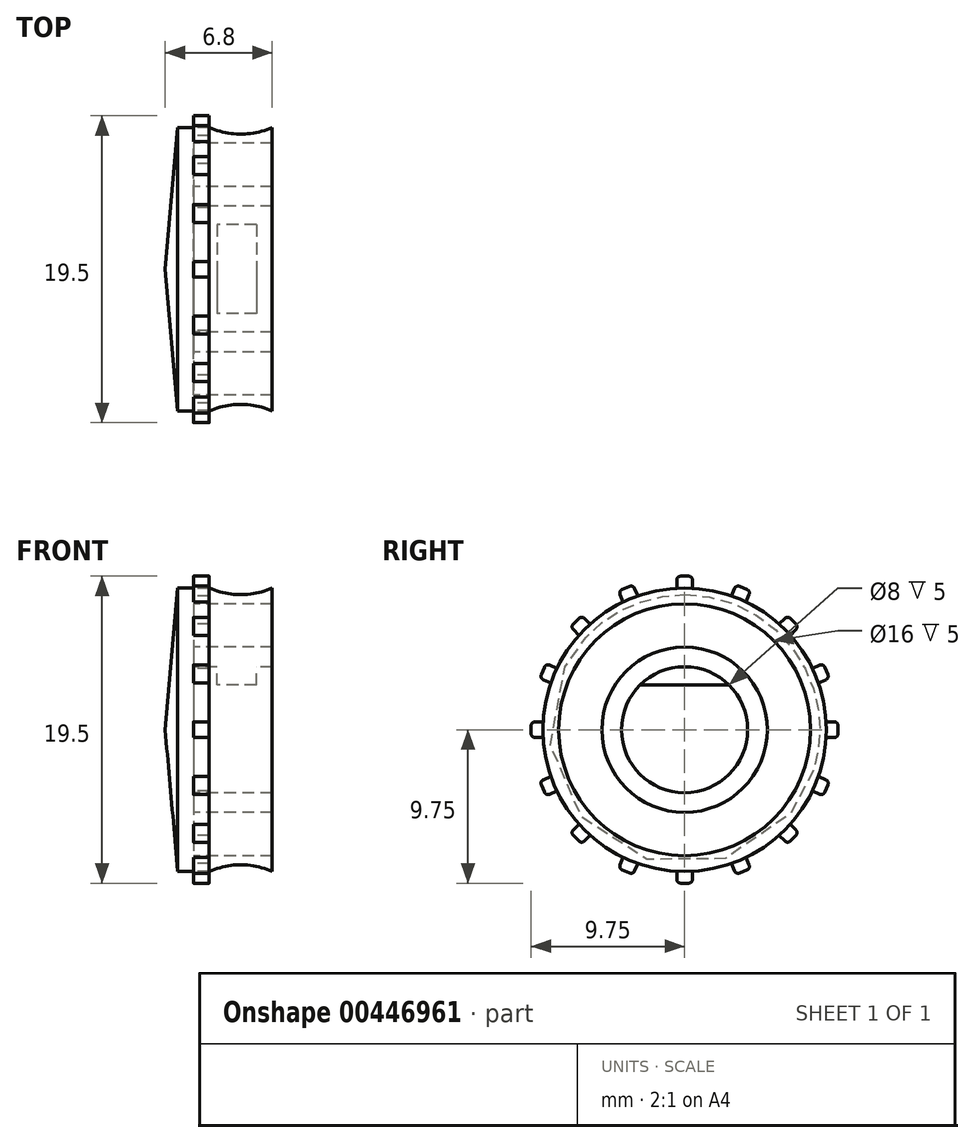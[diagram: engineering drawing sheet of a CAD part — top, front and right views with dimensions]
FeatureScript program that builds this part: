
annotation { "Feature Type Name" : "Feature", "Feature Type Description" : "" }
export const myFeature = defineFeature(function(context is Context, id is Id, definition is map)
    precondition{}
    {
        {
            var Q0;
            Q0=qCreatedBy(makeId("Front.planeOp"),FACE);
            var sketch = newSketch(context, id + "F0", { "sketchPlane" : qUnion([Q0])});
            skLineSegment(sketch, "E0", {"start": v(0, 0) * mm, "end": v(10, 0) * mm, "construction": true});
            skLineSegment(sketch, "E1", {"start": v(-1, 9) * mm, "end": v(0, 9) * mm});
            skLineSegment(sketch, "E2", {"start": v(5, 0) * mm, "end": v(5, 168.85) * mm, "construction": true});
            skLineSegment(sketch, "E3.top", {"start": v(5, 5.25) * mm, "end": v(0, 5.25) * mm});
            skLineSegment(sketch, "E3.left", {"start": v(5, 5.25) * mm, "end": v(5, 4) * mm});
            skLineSegment(sketch, "E4", {"start": v(1, 9) * mm, "end": v(1, 9) * mm});
            skLineSegment(sketch, "E5", {"start": v(1, 9) * mm, "end": v(9, 9) * mm, "construction": true});
            skLineSegment(sketch, "E6", {"start": v(9, 9) * mm, "end": v(41.44, 9) * mm, "construction": true});
            skLineSegment(sketch, "E7", {"start": v(0, 5.25) * mm, "end": v(0, 0) * mm});
            skLineSegment(sketch, "E8", {"start": v(0, 4) * mm, "end": v(0, -2.16) * mm});
            skLineSegment(sketch, "E9", {"start": v(0, 4) * mm, "end": v(5, 4) * mm});
            skLineSegment(sketch, "E10", {"start": v(0, 8) * mm, "end": v(0, 4) * mm});
            skLineSegment(sketch, "E11", {"start": v(0, 0) * mm, "end": v(-1.8, 0) * mm});
            skLineSegment(sketch, "E12", {"start": v(0, 0) * mm, "end": v(0, 37.74) * mm, "construction": true});
            skLineSegment(sketch, "E13", {"start": v(0, 9) * mm, "end": v(1, 9) * mm});
            skLineSegment(sketch, "E14", {"start": v(-1, 9) * mm, "end": v(-1.8, 0) * mm});
            skLineSegment(sketch, "E15", {"start": v(0, 8) * mm, "end": v(5, 8) * mm});
            skLineSegment(sketch, "E16", {"start": v(5, 8) * mm, "end": v(5, 9) * mm});
            skArc(sketch, "E17", {"start": v(1, 9) * mm, "mid": v(3, 8.58) * mm, "end": v(5, 9) * mm});
            skLineSegment(sketch, "E18.top", {"start": v(0, 10.5) * mm, "end": v(1, 10.5) * mm});
            skLineSegment(sketch, "E18.left", {"start": v(0, 9) * mm, "end": v(0, 10.5) * mm});
            skLineSegment(sketch, "E18.right", {"start": v(1, 9) * mm, "end": v(1, 10.5) * mm});
            skSolve(sketch);
        }
        {
            var Q0;
            Q0=makeQuery(id+"F0.imprint","IMPRINT",FACE,{"disambiguationData":[TD([[makeQuery(id+"F0.imprint","IMPRINT",EDGE,{"derivedFrom":sQuery(id+"F0.wireOp",EDGE,"E1")}),-1.0]])]});
            var Q1;
            {var subQ0=sQuery(id+"F0.wireOp",EDGE,"E3.top");Q1=makeQuery(id+"F0.imprint","IMPRINT",FACE,{"disambiguationData":[TD([[makeQuery(id+"F0.imprint","IMPRINT",EDGE,{"derivedFrom":subQ0}),1.0]])]});}
            var Q2;
            Q2=sQuery(id+"F0.wireOp",EDGE,"E0");
            revolve(context, id + "F1", {"entities" : qUnion([Q0, Q1]), "axis" : qUnion([Q2]), "revolveType" : RevolveType.FULL});
        }
        {
            var Q0;
            Q0=qCreatedBy(makeId("Right.planeOp"),FACE);
            var sketch = newSketch(context, id + "F2", { "sketchPlane" : qUnion([Q0])});
            skLineSegment(sketch, "E19", {"start": v(0, 0) * mm, "end": v(0, 9) * mm, "construction": true});
            skLineSegment(sketch, "E20.bottom", {"start": v(-0.5, 8.25) * mm, "end": v(0.5, 8.25) * mm});
            skLineSegment(sketch, "E20.top", {"start": v(-0.25, 9.75) * mm, "end": v(0.25, 9.75) * mm});
            skLineSegment(sketch, "E20.left", {"start": v(-0.5, 8.25) * mm, "end": v(-0.5, 9.5) * mm});
            skLineSegment(sketch, "E20.right", {"start": v(0.5, 8.25) * mm, "end": v(0.5, 9.5) * mm});
            skPoint(sketch, "E20.middle", {"position": v(0, 9) * mm});
            skPoint(sketch, "E21.visualSharp", {"position": v(0.5, 9.75) * mm});
            skArc(sketch, "E21.filletArc", {"start": v(0.5, 9.5) * mm, "mid": v(0.43, 9.68) * mm, "end": v(0.25, 9.75) * mm});
            skPoint(sketch, "E22.visualSharp", {"position": v(-0.5, 9.75) * mm});
            skArc(sketch, "E22.filletArc", {"start": v(-0.25, 9.75) * mm, "mid": v(-0.43, 9.68) * mm, "end": v(-0.5, 9.5) * mm});
            skSolve(sketch);
        }
        {
            var Q0;
            Q0=makeQuery(id+"F2.imprint","IMPRINT",FACE,{"disambiguationData":[TD([[makeQuery(id+"F2.imprint","IMPRINT",EDGE,{"derivedFrom":sQuery(id+"F2.wireOp",EDGE,"E20.bottom")}),1.0]])]});
            extrude(context, id + "F3", {"entities" : qUnion([Q0]), "operationType" : NewBodyOperationType.ADD, "depth" : 1 * mm});
        }
        {
            var Q0;
            Q0=makeQuery(id+"F3.opExtrude","SWEPT_FACE",FACE,{"disambiguationData":[OSD([sQuery(id+"F2.wireOp",EDGE,"E20.top")])]});
            var Q1;
            Q1=makeQuery(id+"F3.opExtrude","CAP_FACE",FACE,{"disambiguationData":[OSD([sQuery(id+"F2.wireOp",EDGE,"E20.bottom"),sQuery(id+"F2.wireOp",EDGE,"E20.top"),sQuery(id+"F2.wireOp",EDGE,"E20.left"),sQuery(id+"F2.wireOp",EDGE,"E20.right"),sQuery(id+"F2.wireOp",EDGE,"E21.filletArc"),sQuery(id+"F2.wireOp",EDGE,"E22.filletArc")])],"isStart":true});
            var Q2;
            Q2=makeQuery(id+"F3.opExtrude","SWEPT_FACE",FACE,{"disambiguationData":[OSD([sQuery(id+"F2.wireOp",EDGE,"E22.filletArc")])]});
            var Q3;
            Q3=makeQuery(id+"F3.opExtrude","SWEPT_FACE",FACE,{"disambiguationData":[OSD([sQuery(id+"F2.wireOp",EDGE,"E21.filletArc")])]});
            var Q4;
            Q4=makeQuery(id+"F3.opExtrude","CAP_FACE",FACE,{"disambiguationData":[OSD([sQuery(id+"F2.wireOp",EDGE,"E20.bottom"),sQuery(id+"F2.wireOp",EDGE,"E20.top"),sQuery(id+"F2.wireOp",EDGE,"E20.left"),sQuery(id+"F2.wireOp",EDGE,"E20.right"),sQuery(id+"F2.wireOp",EDGE,"E21.filletArc"),sQuery(id+"F2.wireOp",EDGE,"E22.filletArc")])],"isStart":false});
            var Q5;
            Q5=makeQuery(id+"F3.opExtrude","SWEPT_FACE",FACE,{"disambiguationData":[OSD([sQuery(id+"F2.wireOp",EDGE,"E20.left")])]});
            var Q6;
            Q6=makeQuery(id+"F3.opExtrude","SWEPT_FACE",FACE,{"disambiguationData":[OSD([sQuery(id+"F2.wireOp",EDGE,"E20.right")])]});
            var Q7;
            Q7=makeQuery(id+"F1.opRevolve","SWEPT_EDGE",EDGE,{"disambiguationData":[OSD([sQuery(id+"F0.wireOp",EDGE,"E1"),sQuery(id+"F0.wireOp",EDGE,"E14")])]});
            circularPattern(context, id + "F4", {"patternType" : PatternType.FACE, "faces" : qUnion([Q0, Q1, Q2, Q3, Q4, Q5, Q6]), "axis" : qUnion([Q7]), "angle" : 22.5 * degree, "instanceCount" : 16, "computeTransformsWithoutBuiltin" : true});
        }
        {
            var Q0;
            Q0=qCreatedBy(makeId("Right.planeOp"),FACE);
            cPlane(context, id + "F5", {"entities" : qUnion([Q0]), "cplaneType" : CPlaneType.OFFSET, "offset" : 4 * mm, "width" : 150 * mm, "height" : 150 * mm});
        }
        {
            var Q0;
            Q0=qCreatedBy(id+"F5.planeOp",FACE);
            var sketch = newSketch(context, id + "F6", { "sketchPlane" : qUnion([Q0])});
            skLineSegment(sketch, "E23", {"start": v(0, 0) * mm, "end": v(0, 4.99) * mm, "construction": true});
            skLineSegment(sketch, "E24", {"start": v(0, 4.99) * mm, "end": v(0, 2.83) * mm, "construction": true});
            skLineSegment(sketch, "E25", {"start": v(0, 2.83) * mm, "end": v(4, 2.83) * mm, "construction": true});
            skLineSegment(sketch, "E26", {"start": v(0, 2.83) * mm, "end": v(-3.25, 2.83) * mm});
            skArc(sketch, "E27", {"start": v(3.47, 2.83) * mm, "mid": v(0.1, 4.5) * mm, "end": v(-3.25, 2.83) * mm});
            skLineSegment(sketch, "E28", {"start": v(0, 2.83) * mm, "end": v(3.47, 2.83) * mm});
            skSolve(sketch);
        }
        {
            var Q0;
            Q0=makeQuery(id+"F6.imprint","IMPRINT",FACE,{"disambiguationData":[TD([[makeQuery(id+"F6.imprint","IMPRINT",EDGE,{"derivedFrom":sQuery(id+"F6.wireOp",EDGE,"E26")}),-1.0]])]});
            extrude(context, id + "F7", {"entities" : qUnion([Q0]), "operationType" : NewBodyOperationType.ADD, "oppositeDirection" : true, "depth" : 2.5 * mm, "offsetDistance" : 25 * mm});
        }
    });
